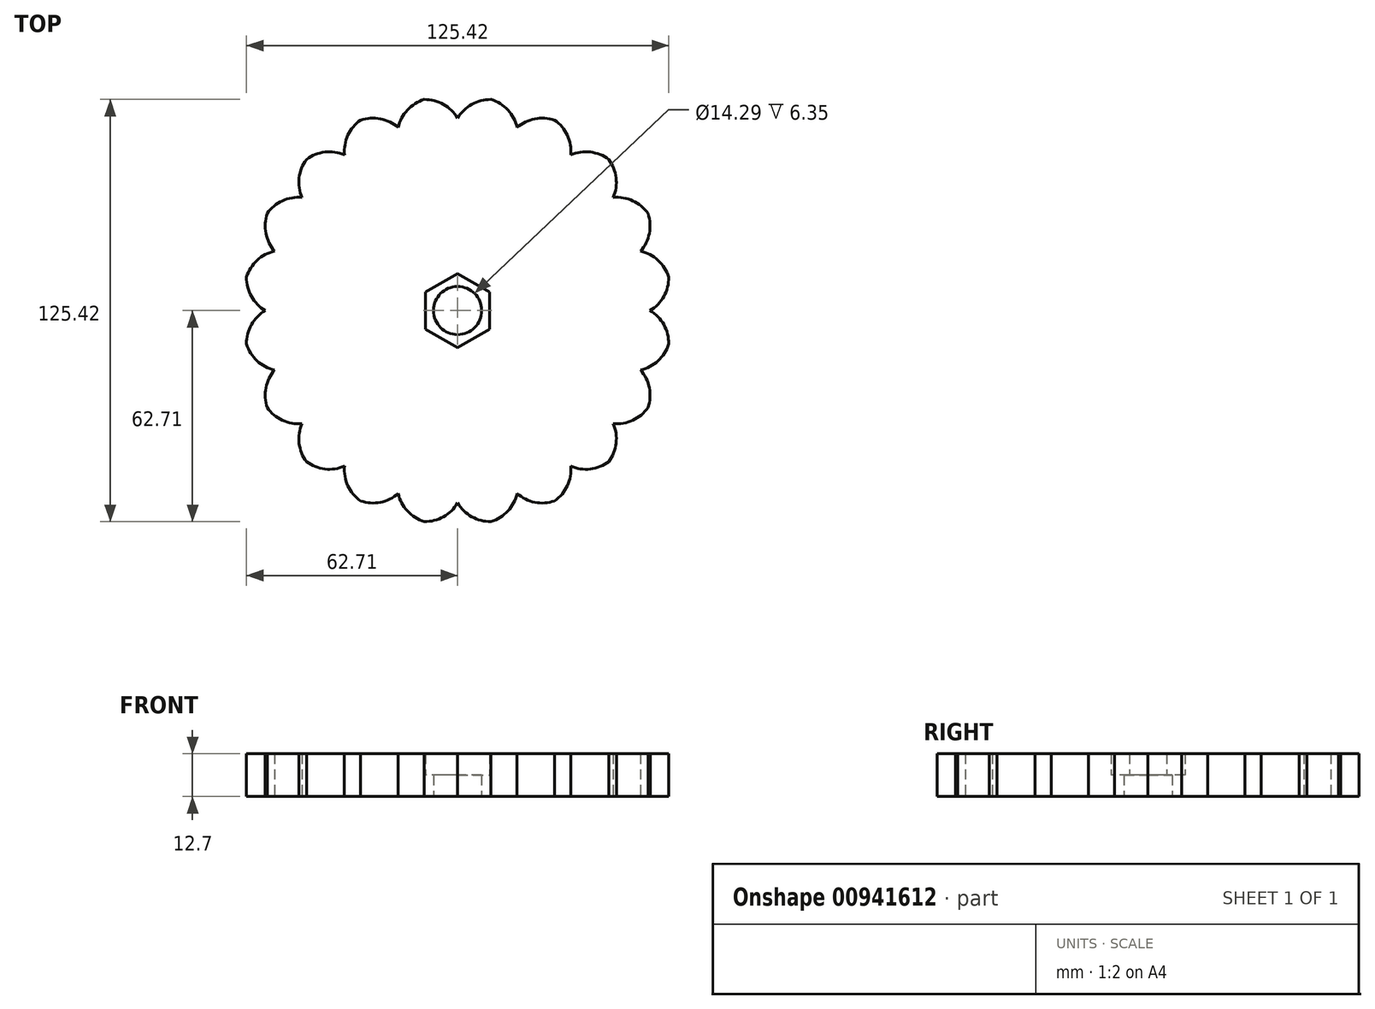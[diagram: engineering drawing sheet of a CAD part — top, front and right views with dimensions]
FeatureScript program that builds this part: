
annotation { "Feature Type Name" : "Feature", "Feature Type Description" : "" }
export const myFeature = defineFeature(function(context is Context, id is Id, definition is map)
    precondition{}
    {
        {
            assignVariable(context, id + "F0", {"name" : "levelerThickness", "anyValue" : 12.7 * mm});
        }
        {
            var Q0;
            Q0=qCreatedBy(makeId("Top.planeOp"),FACE);
            var sketch = newSketch(context, id + "F1", { "sketchPlane" : qUnion([Q0])});
            skCircle(sketch, "E0", {"center": v(0, 0) * mm, "radius": 63.5 * mm});
            skCircle(sketch, "E1", {"center": v(0, 0) * mm, "radius": 7.14 * mm});
            skCircle(sketch, "E2.cCircle", {"center": v(0, 0) * mm, "radius": 9.53 * mm, "construction": true});
            skLineSegment(sketch, "E2.0", {"start": v(9.52, 5.5) * mm, "end": v(9.52, -5.5) * mm});
            skLineSegment(sketch, "E2.1", {"start": v(9.52, -5.5) * mm, "end": v(0, -11) * mm});
            skLineSegment(sketch, "E2.2", {"start": v(0, -11) * mm, "end": v(-9.52, -5.5) * mm});
            skLineSegment(sketch, "E2.3", {"start": v(-9.52, -5.5) * mm, "end": v(-9.52, 5.5) * mm});
            skLineSegment(sketch, "E2.4", {"start": v(-9.52, 5.5) * mm, "end": v(0, 11) * mm});
            skLineSegment(sketch, "E2.5", {"start": v(0, 11) * mm, "end": v(9.52, 5.5) * mm});
            skPoint(sketch, "E2.0.midPoint", {"position": v(9.52, 0) * mm});
            skPoint(sketch, "E3", {"position": v(0, 57.15) * mm});
            skArc(sketch, "E4", {"start": v(0, 57.15) * mm, "mid": v(-4.23, 61.28) * mm, "end": v(-9.97, 62.71) * mm});
            skLineSegment(sketch, "E5", {"start": v(-9.97, 62.71) * mm, "end": v(9.97, 62.71) * mm, "construction": true});
            skPoint(sketch, "E6", {"position": v(0, 62.71) * mm});
            skArc(sketch, "E7", {"start": v(9.97, 62.71) * mm, "mid": v(4.23, 61.28) * mm, "end": v(0, 57.15) * mm});
            skArc(sketch, "E8.1.0", {"start": v(-17.66, 54.35) * mm, "mid": v(-22.96, 56.97) * mm, "end": v(-28.87, 56.56) * mm});
            skArc(sketch, "E8.1.1", {"start": v(-9.9, 62.72) * mm, "mid": v(-14.91, 59.6) * mm, "end": v(-17.66, 54.35) * mm});
            skArc(sketch, "E8.2.0", {"start": v(-33.6, 46.24) * mm, "mid": v(-39.45, 47.09) * mm, "end": v(-44.93, 44.87) * mm});
            skArc(sketch, "E8.2.1", {"start": v(-28.8, 56.6) * mm, "mid": v(-32.6, 52.07) * mm, "end": v(-33.6, 46.24) * mm});
            skArc(sketch, "E8.3.0", {"start": v(-46.24, 33.6) * mm, "mid": v(-52.07, 32.6) * mm, "end": v(-56.6, 28.8) * mm});
            skArc(sketch, "E8.3.1", {"start": v(-44.87, 44.93) * mm, "mid": v(-47.09, 39.45) * mm, "end": v(-46.24, 33.6) * mm});
            skArc(sketch, "E8.4.0", {"start": v(-54.35, 17.66) * mm, "mid": v(-59.6, 14.91) * mm, "end": v(-62.72, 9.9) * mm});
            skArc(sketch, "E8.4.1", {"start": v(-56.56, 28.87) * mm, "mid": v(-56.97, 22.96) * mm, "end": v(-54.35, 17.66) * mm});
            skArc(sketch, "E8.5.0", {"start": v(-57.15, 0) * mm, "mid": v(-61.28, -4.23) * mm, "end": v(-62.71, -9.97) * mm});
            skArc(sketch, "E8.5.1", {"start": v(-62.71, 9.97) * mm, "mid": v(-61.28, 4.23) * mm, "end": v(-57.15, 0) * mm});
            skArc(sketch, "E8.6.0", {"start": v(-54.35, -17.66) * mm, "mid": v(-56.97, -22.96) * mm, "end": v(-56.56, -28.87) * mm});
            skArc(sketch, "E8.6.1", {"start": v(-62.72, -9.9) * mm, "mid": v(-59.6, -14.91) * mm, "end": v(-54.35, -17.66) * mm});
            skArc(sketch, "E8.7.0", {"start": v(-46.24, -33.6) * mm, "mid": v(-47.09, -39.45) * mm, "end": v(-44.87, -44.93) * mm});
            skArc(sketch, "E8.7.1", {"start": v(-56.6, -28.8) * mm, "mid": v(-52.07, -32.6) * mm, "end": v(-46.24, -33.6) * mm});
            skArc(sketch, "E8.8.0", {"start": v(-33.6, -46.24) * mm, "mid": v(-32.6, -52.07) * mm, "end": v(-28.8, -56.6) * mm});
            skArc(sketch, "E8.8.1", {"start": v(-44.93, -44.87) * mm, "mid": v(-39.45, -47.09) * mm, "end": v(-33.6, -46.24) * mm});
            skArc(sketch, "E8.9.0", {"start": v(-17.66, -54.35) * mm, "mid": v(-14.91, -59.6) * mm, "end": v(-9.9, -62.72) * mm});
            skArc(sketch, "E8.9.1", {"start": v(-28.87, -56.56) * mm, "mid": v(-22.96, -56.97) * mm, "end": v(-17.66, -54.35) * mm});
            skArc(sketch, "E8.10.0", {"start": v(0, -57.15) * mm, "mid": v(4.23, -61.28) * mm, "end": v(9.97, -62.71) * mm});
            skArc(sketch, "E8.10.1", {"start": v(-9.97, -62.71) * mm, "mid": v(-4.23, -61.28) * mm, "end": v(0, -57.15) * mm});
            skArc(sketch, "E8.11.0", {"start": v(17.66, -54.35) * mm, "mid": v(22.96, -56.97) * mm, "end": v(28.87, -56.56) * mm});
            skArc(sketch, "E8.11.1", {"start": v(9.9, -62.72) * mm, "mid": v(14.91, -59.6) * mm, "end": v(17.66, -54.35) * mm});
            skArc(sketch, "E8.12.0", {"start": v(33.6, -46.24) * mm, "mid": v(39.45, -47.09) * mm, "end": v(44.93, -44.87) * mm});
            skArc(sketch, "E8.12.1", {"start": v(28.8, -56.6) * mm, "mid": v(32.6, -52.07) * mm, "end": v(33.6, -46.24) * mm});
            skArc(sketch, "E8.13.0", {"start": v(46.24, -33.6) * mm, "mid": v(52.07, -32.6) * mm, "end": v(56.6, -28.8) * mm});
            skArc(sketch, "E8.13.1", {"start": v(44.87, -44.93) * mm, "mid": v(47.09, -39.45) * mm, "end": v(46.24, -33.6) * mm});
            skArc(sketch, "E8.14.0", {"start": v(54.35, -17.66) * mm, "mid": v(59.6, -14.91) * mm, "end": v(62.72, -9.9) * mm});
            skArc(sketch, "E8.14.1", {"start": v(56.56, -28.87) * mm, "mid": v(56.97, -22.96) * mm, "end": v(54.35, -17.66) * mm});
            skArc(sketch, "E8.15.0", {"start": v(57.15, 0) * mm, "mid": v(61.28, 4.23) * mm, "end": v(62.71, 9.97) * mm});
            skArc(sketch, "E8.15.1", {"start": v(62.71, -9.97) * mm, "mid": v(61.28, -4.23) * mm, "end": v(57.15, 0) * mm});
            skArc(sketch, "E8.16.0", {"start": v(54.35, 17.66) * mm, "mid": v(56.97, 22.96) * mm, "end": v(56.56, 28.87) * mm});
            skArc(sketch, "E8.16.1", {"start": v(62.72, 9.9) * mm, "mid": v(59.6, 14.91) * mm, "end": v(54.35, 17.66) * mm});
            skArc(sketch, "E8.17.0", {"start": v(46.24, 33.6) * mm, "mid": v(47.09, 39.45) * mm, "end": v(44.87, 44.93) * mm});
            skArc(sketch, "E8.17.1", {"start": v(56.6, 28.8) * mm, "mid": v(52.07, 32.6) * mm, "end": v(46.24, 33.6) * mm});
            skArc(sketch, "E8.18.0", {"start": v(33.6, 46.24) * mm, "mid": v(32.6, 52.07) * mm, "end": v(28.8, 56.6) * mm});
            skArc(sketch, "E8.18.1", {"start": v(44.93, 44.87) * mm, "mid": v(39.45, 47.09) * mm, "end": v(33.6, 46.24) * mm});
            skArc(sketch, "E8.19.0", {"start": v(17.66, 54.35) * mm, "mid": v(14.91, 59.6) * mm, "end": v(9.9, 62.72) * mm});
            skArc(sketch, "E8.19.1", {"start": v(28.87, 56.56) * mm, "mid": v(22.96, 56.97) * mm, "end": v(17.66, 54.35) * mm});
            skSolve(sketch);
        }
        {
            var Q0;
            Q0=makeQuery(id+"F1.imprint","IMPRINT",FACE,{"disambiguationData":[TD([[makeQuery(id+"F1.imprint","IMPRINT",EDGE,{"derivedFrom":sQuery(id+"F1.wireOp",EDGE,"E2.0")}),1.0]])]});
            extrude(context, id + "F2", {"entities" : qUnion([Q0]), "depth" : getVariable(context, 'levelerThickness'), "offsetDistance" : 25.4 * mm});
        }
        {
            var Q0;
            Q0=makeQuery(id+"F1.imprint","IMPRINT",FACE,{"disambiguationData":[TD([[makeQuery(id+"F1.imprint","IMPRINT",EDGE,{"derivedFrom":sQuery(id+"F1.wireOp",EDGE,"E1")}),-1.0]])]});
            extrude(context, id + "F3", {"entities" : qUnion([Q0]), "operationType" : NewBodyOperationType.ADD, "depth" : getVariable(context, 'levelerThickness') / 2, "offsetDistance" : 25.4 * mm});
        }
    });
